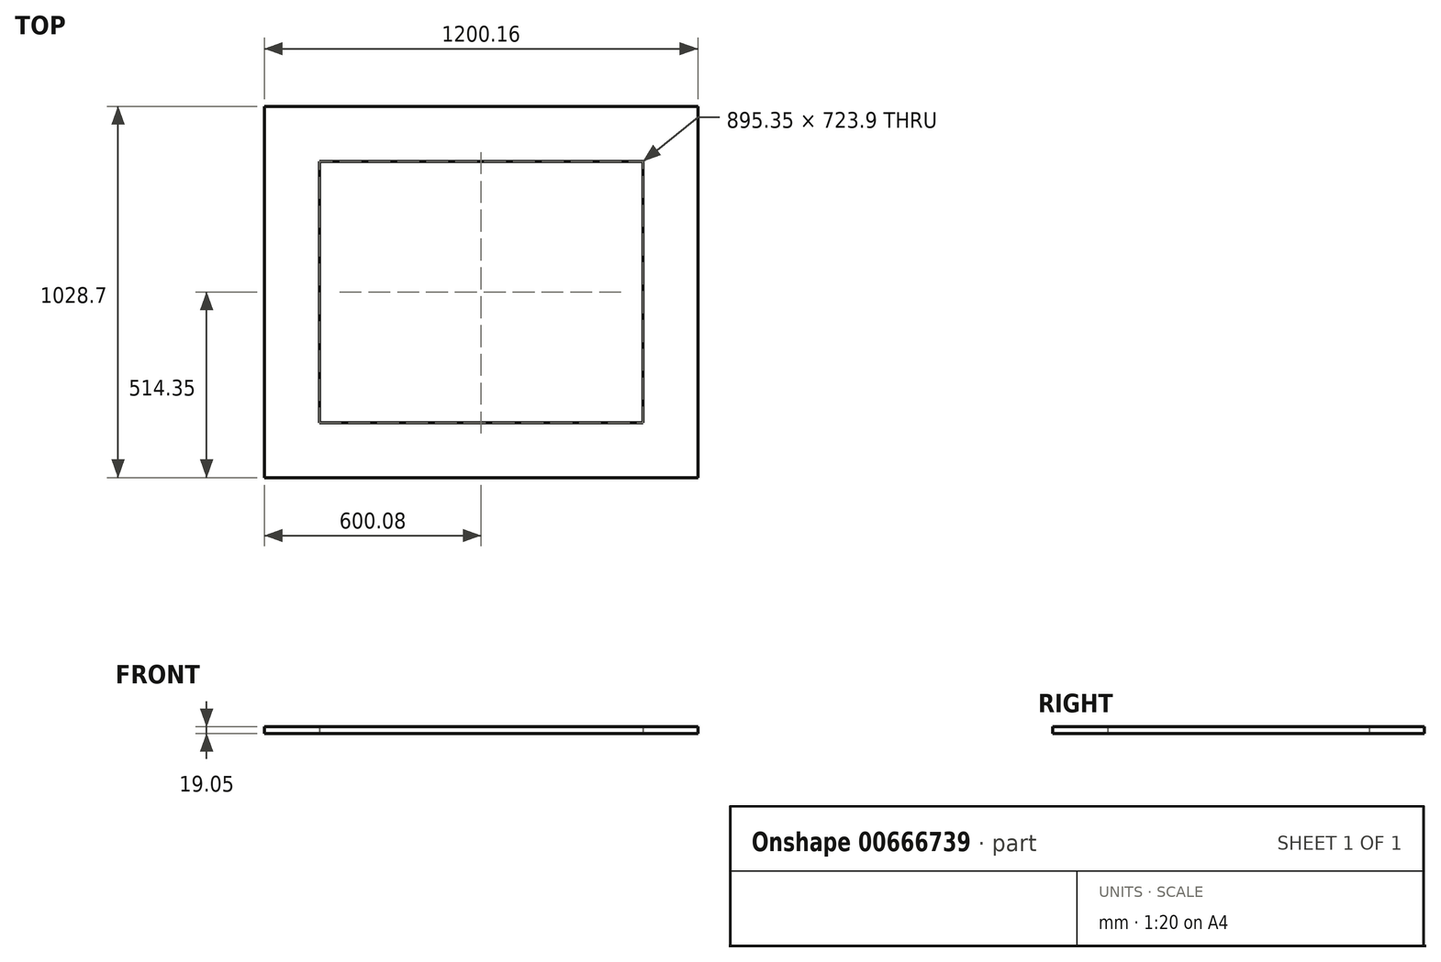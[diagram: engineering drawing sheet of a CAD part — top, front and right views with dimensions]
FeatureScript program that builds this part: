
annotation { "Feature Type Name" : "Feature", "Feature Type Description" : "" }
export const myFeature = defineFeature(function(context is Context, id is Id, definition is map)
    precondition{}
    {
        {
            var Q0;
            Q0=qCreatedBy(makeId("Top.planeOp"),FACE);
            var sketch = newSketch(context, id + "F0", { "sketchPlane" : qUnion([Q0])});
            skLineSegment(sketch, "E0.bottom", {"start": v(-600.08, 514.35) * mm, "end": v(600.08, 514.35) * mm});
            skLineSegment(sketch, "E0.top", {"start": v(-600.08, -514.35) * mm, "end": v(600.07, -514.35) * mm});
            skLineSegment(sketch, "E0.left", {"start": v(-600.08, 514.35) * mm, "end": v(-600.08, -514.35) * mm});
            skLineSegment(sketch, "E0.right", {"start": v(600.08, 514.35) * mm, "end": v(600.07, -514.35) * mm});
            skPoint(sketch, "E0.middle", {"position": v(0, 0) * mm});
            skLineSegment(sketch, "E1", {"start": v(-600.08, 514.35) * mm, "end": v(-447.68, 514.35) * mm});
            skLineSegment(sketch, "E2", {"start": v(-447.68, 514.35) * mm, "end": v(-447.68, 361.95) * mm});
            skLineSegment(sketch, "E3", {"start": v(600.07, -514.35) * mm, "end": v(447.67, -514.35) * mm});
            skLineSegment(sketch, "E4", {"start": v(447.67, -514.35) * mm, "end": v(447.67, -361.95) * mm});
            skLineSegment(sketch, "E5.bottom", {"start": v(-447.68, 361.95) * mm, "end": v(447.67, 361.95) * mm});
            skLineSegment(sketch, "E5.top", {"start": v(-447.68, -361.95) * mm, "end": v(447.67, -361.95) * mm});
            skLineSegment(sketch, "E5.left", {"start": v(-447.68, 361.95) * mm, "end": v(-447.68, -361.95) * mm});
            skLineSegment(sketch, "E5.right", {"start": v(447.67, 361.95) * mm, "end": v(447.67, -361.95) * mm});
            skSolve(sketch);
        }
        {
            var Q0;
            Q0=makeQuery(id+"F0.imprint","IMPRINT",FACE,{"disambiguationData":[TD([[makeQuery(id+"F0.imprint","IMPRINT",EDGE,{"derivedFrom":sQuery(id+"F0.wireOp",EDGE,"E0.bottom")}),-1.0]])]});
            var Q1;
            Q1=makeQuery(id+"F0.imprint","IMPRINT",FACE,{"disambiguationData":[TD([[makeQuery(id+"F0.imprint","IMPRINT",EDGE,{"derivedFrom":sQuery(id+"F0.wireOp",EDGE,"E0.top")}),1.0]])]});
            extrude(context, id + "F1", {"entities" : qUnion([Q0, Q1]), "depth" : 19.05 * mm, "offsetDistance" : 25.4 * mm});
        }
    });
